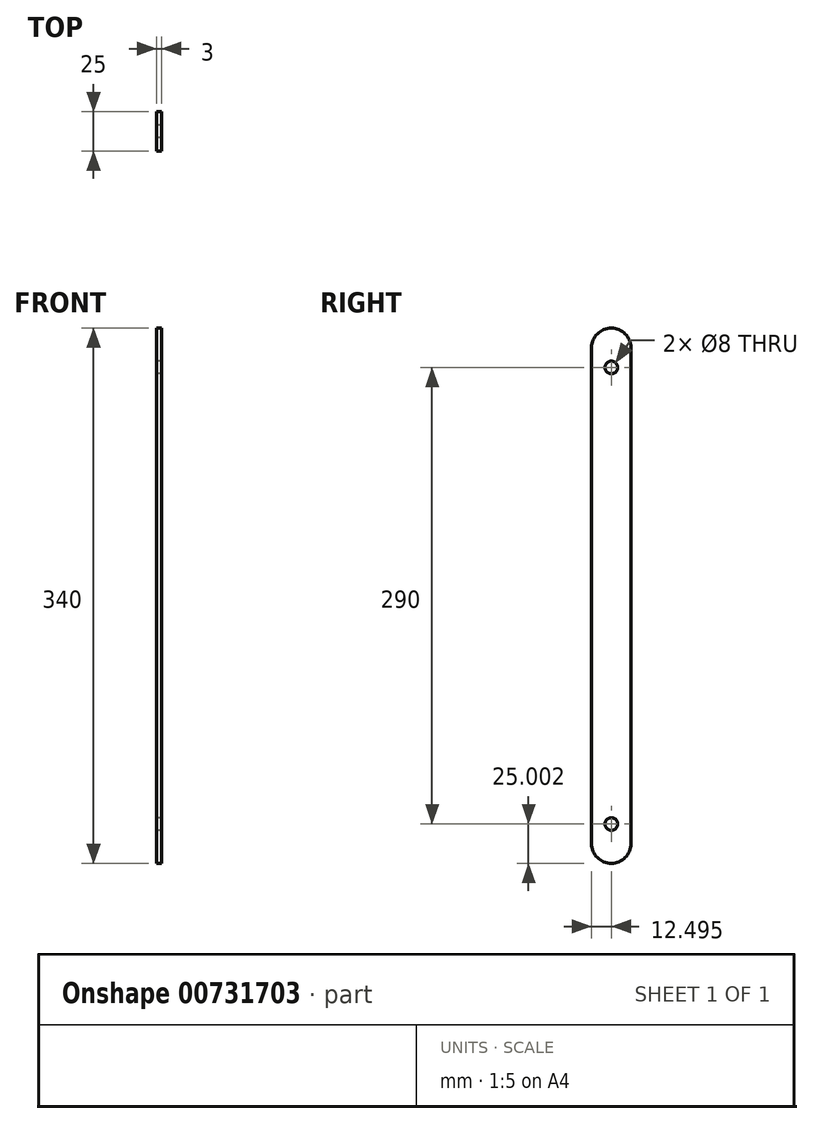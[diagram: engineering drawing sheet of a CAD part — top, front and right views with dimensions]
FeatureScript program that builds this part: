
annotation { "Feature Type Name" : "Feature", "Feature Type Description" : "" }
export const myFeature = defineFeature(function(context is Context, id is Id, definition is map)
    precondition{}
    {
        {
            var Q0;
            Q0=qCreatedBy(makeId("Right.planeOp"),FACE);
            var sketch = newSketch(context, id + "F0", { "sketchPlane" : qUnion([Q0])});
            skLineSegment(sketch, "E0.bottom", {"start": v(-167.07, -214.59) * mm, "end": v(-167.07, -214.59) * mm});
            skLineSegment(sketch, "E0.top", {"start": v(-167.07, 125.41) * mm, "end": v(-167.07, 125.41) * mm});
            skLineSegment(sketch, "E0.left", {"start": v(-179.57, -202.09) * mm, "end": v(-179.57, 112.91) * mm});
            skLineSegment(sketch, "E0.right", {"start": v(-154.57, -202.09) * mm, "end": v(-154.57, 112.91) * mm});
            skCircle(sketch, "E1", {"center": v(-167.07, 100.41) * mm, "radius": 4 * mm});
            skCircle(sketch, "E2", {"center": v(-167.07, -189.59) * mm, "radius": 4 * mm});
            skPoint(sketch, "E3.visualSharp", {"position": v(-179.57, 125.41) * mm});
            skArc(sketch, "E3.filletArc", {"start": v(-167.07, 125.41) * mm, "mid": v(-175.91, 121.75) * mm, "end": v(-179.57, 112.91) * mm});
            skPoint(sketch, "E4.visualSharp", {"position": v(-154.57, 125.41) * mm});
            skArc(sketch, "E4.filletArc", {"start": v(-154.57, 112.91) * mm, "mid": v(-158.24, 121.75) * mm, "end": v(-167.07, 125.41) * mm});
            skPoint(sketch, "E5.visualSharp", {"position": v(-179.57, -214.59) * mm});
            skArc(sketch, "E5.filletArc", {"start": v(-179.57, -202.09) * mm, "mid": v(-175.91, -210.93) * mm, "end": v(-167.07, -214.59) * mm});
            skPoint(sketch, "E6.visualSharp", {"position": v(-154.57, -214.59) * mm});
            skArc(sketch, "E6.filletArc", {"start": v(-167.07, -214.59) * mm, "mid": v(-158.24, -210.93) * mm, "end": v(-154.57, -202.09) * mm});
            skSolve(sketch);
        }
        {
            var Q0;
            Q0 = qSketchRegion(id + "F0", true);
            extrude(context, id + "F1", {"entities" : qUnion([Q0]), "depth" : 3 * mm, "offsetDistance" : 25 * mm});
        }
    });
